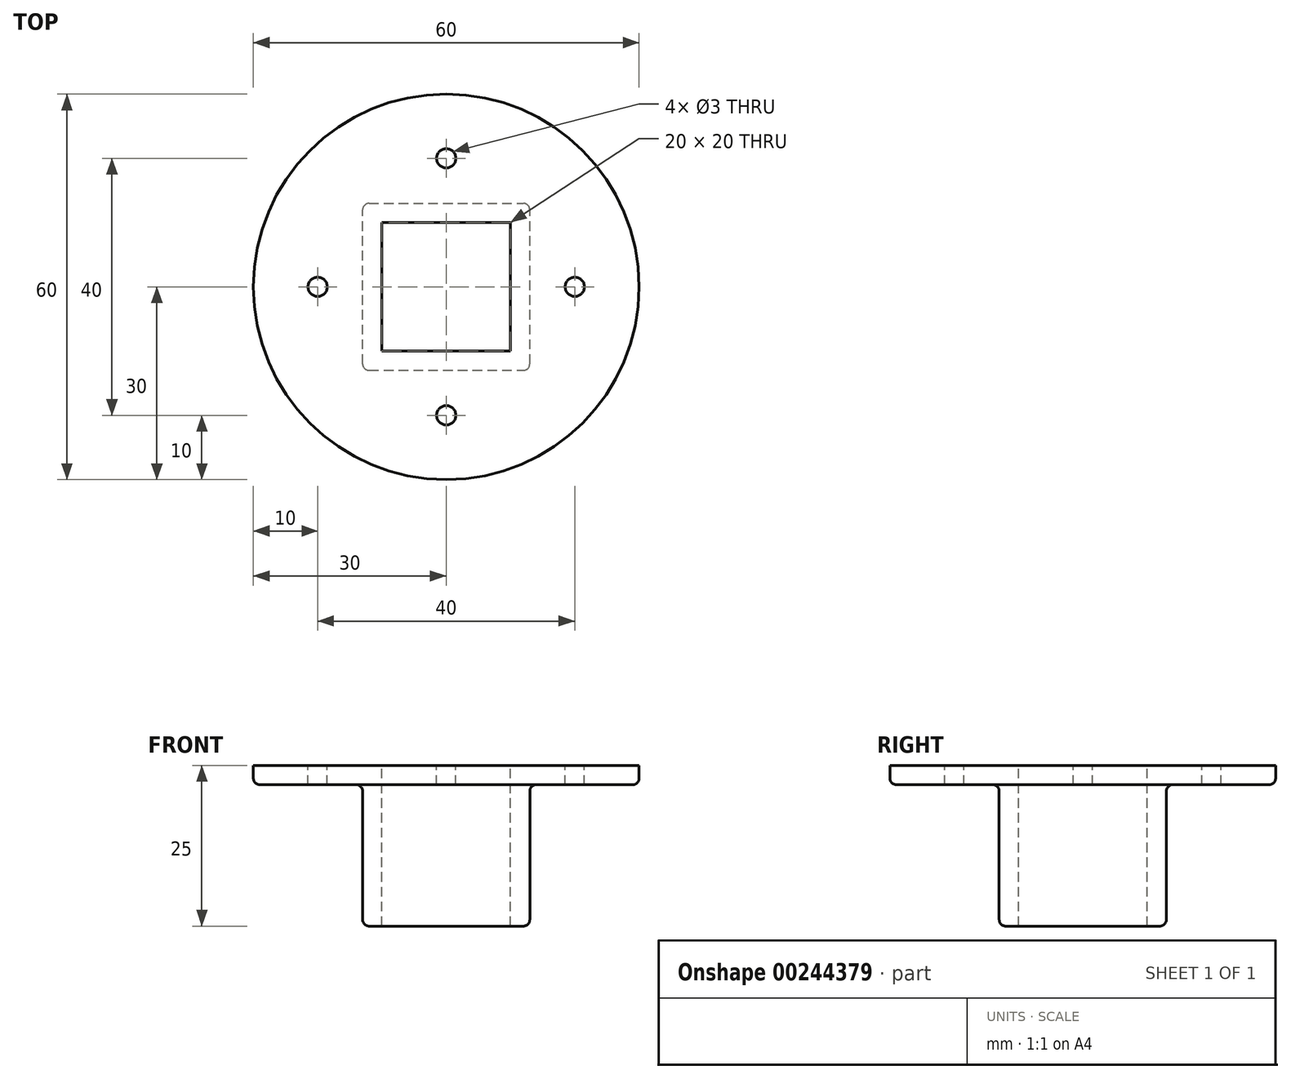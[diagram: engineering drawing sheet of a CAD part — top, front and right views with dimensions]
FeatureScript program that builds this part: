
annotation { "Feature Type Name" : "Feature", "Feature Type Description" : "" }
export const myFeature = defineFeature(function(context is Context, id is Id, definition is map)
    precondition{}
    {
        {
            var Q0;
            Q0=qCreatedBy(makeId("Top.planeOp"),FACE);
            var sketch = newSketch(context, id + "F0", { "sketchPlane" : qUnion([Q0])});
            skLineSegment(sketch, "E0.bottom", {"start": v(0, 0) * mm, "end": v(20, 0) * mm});
            skLineSegment(sketch, "E0.top", {"start": v(0, 20) * mm, "end": v(20, 20) * mm});
            skLineSegment(sketch, "E0.left", {"start": v(0, 0) * mm, "end": v(0, 20) * mm});
            skLineSegment(sketch, "E0.right", {"start": v(20, 0) * mm, "end": v(20, 20) * mm});
            skLineSegment(sketch, "E1.bottom", {"start": v(-3, -3) * mm, "end": v(23, -3) * mm});
            skLineSegment(sketch, "E1.top", {"start": v(-3, 23) * mm, "end": v(23, 23) * mm});
            skLineSegment(sketch, "E1.left", {"start": v(-3, -3) * mm, "end": v(-3, 23) * mm});
            skLineSegment(sketch, "E1.right", {"start": v(23, -3) * mm, "end": v(23, 23) * mm});
            skCircle(sketch, "E2", {"center": v(10, 10) * mm, "radius": 30 * mm});
            skPoint(sketch, "E2.centerSnap0", {"position": v(0, 10) * mm});
            skPoint(sketch, "E2.centerSnap1", {"position": v(10, 0) * mm});
            skSolve(sketch);
        }
        {
            var Q0;
            Q0 = qSketchRegion(id + "F0", true);
            extrude(context, id + "F1", {"entities" : qUnion([Q0]), "oppositeDirection" : true, "depth" : 3 * mm});
        }
        {
            var Q0;
            Q0=makeQuery(id+"F0.imprint","IMPRINT",FACE,{"disambiguationData":[TD([[makeQuery(id+"F0.imprint","IMPRINT",EDGE,{"derivedFrom":sQuery(id+"F0.wireOp",EDGE,"E0.bottom")}),-1.0]])]});
            extrude(context, id + "F2", {"entities" : qUnion([Q0]), "operationType" : NewBodyOperationType.ADD, "oppositeDirection" : true, "depth" : 25 * mm});
        }
        {
            var Q0;
            Q0=makeQuery(id+"F1.opExtrude","CAP_FACE",FACE,{"disambiguationData":[OSD([sQuery(id+"F0.wireOp",EDGE,"E1.bottom"),sQuery(id+"F0.wireOp",EDGE,"E1.top"),sQuery(id+"F0.wireOp",EDGE,"E1.left"),sQuery(id+"F0.wireOp",EDGE,"E1.right"),sQuery(id+"F0.wireOp",EDGE,"E2")])],"isStart":false});
            var Q1;
            Q1=makeQuery(id+"F2.opExtrude","SWEPT_FACE",FACE,{"disambiguationData":[OSD([sQuery(id+"F0.wireOp",EDGE,"E1.top")])]});
            var Q2;
            Q2=makeQuery(id+"F2.opExtrude","SWEPT_FACE",FACE,{"disambiguationData":[OSD([sQuery(id+"F0.wireOp",EDGE,"E1.right")])]});
            var Q3;
            Q3=makeQuery(id+"F2.opExtrude","SWEPT_FACE",FACE,{"disambiguationData":[OSD([sQuery(id+"F0.wireOp",EDGE,"E1.bottom")])]});
            var Q4;
            Q4=makeQuery(id+"F2.opExtrude","SWEPT_FACE",FACE,{"disambiguationData":[OSD([sQuery(id+"F0.wireOp",EDGE,"E1.left")])]});
            fillet(context, id + "F3", {"entities" : qUnion([Q0, Q1, Q2, Q3, Q4]), "radius" : 1 * mm, "tangentPropagation" : true, "allowEdgeOverflow" : false});
        }
        {
            var Q0;
            {var subQ0=sQuery(id+"F0.wireOp",EDGE,"E1.right");var subQ1=sQuery(id+"F0.wireOp",EDGE,"E1.left");var subQ2=sQuery(id+"F0.wireOp",EDGE,"E1.top");var subQ3=sQuery(id+"F0.wireOp",EDGE,"E1.bottom");Q0=makeQuery(id+"F2.boolean.opBoolean","MERGE",FACE,{"derivedFrom":[makeQuery(id+"F1.opExtrude","CAP_FACE",FACE,{"disambiguationData":[OSD([subQ3,subQ2,subQ1,subQ0,sQuery(id+"F0.wireOp",EDGE,"E2")])],"isStart":true}),makeQuery(id+"F2.opExtrude","CAP_FACE",FACE,{"disambiguationData":[OSD([sQuery(id+"F0.wireOp",EDGE,"E0.bottom"),sQuery(id+"F0.wireOp",EDGE,"E0.top"),sQuery(id+"F0.wireOp",EDGE,"E0.left"),sQuery(id+"F0.wireOp",EDGE,"E0.right"),subQ3,subQ2,subQ1,subQ0])],"isStart":true})]});}
            var sketch = newSketch(context, id + "F4", { "sketchPlane" : qUnion([Q0])});
            skPoint(sketch, "E3", {"position": v(10, 30) * mm});
            skPoint(sketch, "E3.positionSnap0", {"position": v(10, 20) * mm});
            skPoint(sketch, "E4", {"position": v(10, 10) * mm});
            skPoint(sketch, "E5.1.0", {"position": v(-10, 10) * mm});
            skPoint(sketch, "E5.2.0", {"position": v(10, -10) * mm});
            skPoint(sketch, "E5.3.0", {"position": v(30, 10) * mm});
            skSolve(sketch);
        }
        {
            var Q0;
            Q0=sQuery(id+"F4.wireOp",VERTEX,"E3");
            var Q1;
            Q1=sQuery(id+"F4.wireOp",VERTEX,"E5.3.0");
            var Q2;
            Q2=sQuery(id+"F4.wireOp",VERTEX,"E5.2.0");
            var Q3;
            Q3=sQuery(id+"F4.wireOp",VERTEX,"E5.1.0");
            var Q4;
            Q4=makeQuery(id+"F1.opExtrude","SWEPT_BODY",BODY,{"disambiguationData":[OSD([sQuery(id+"F0.wireOp",EDGE,"E1.bottom"),sQuery(id+"F0.wireOp",EDGE,"E1.top"),sQuery(id+"F0.wireOp",EDGE,"E1.left"),sQuery(id+"F0.wireOp",EDGE,"E1.right"),sQuery(id+"F0.wireOp",EDGE,"E2")])]});
            hole(context, id + "F5", {"style" : HoleStyle.SIMPLE, "endStyle" : HoleEndStyle.THROUGH, "holeDiameter" : 3 * mm, "tappedDepth" : 12 * mm, "tapClearance" : 3, "locations" : qUnion([Q0, Q1, Q2, Q3]), "scope" : qUnion([Q4])});
        }
    });
